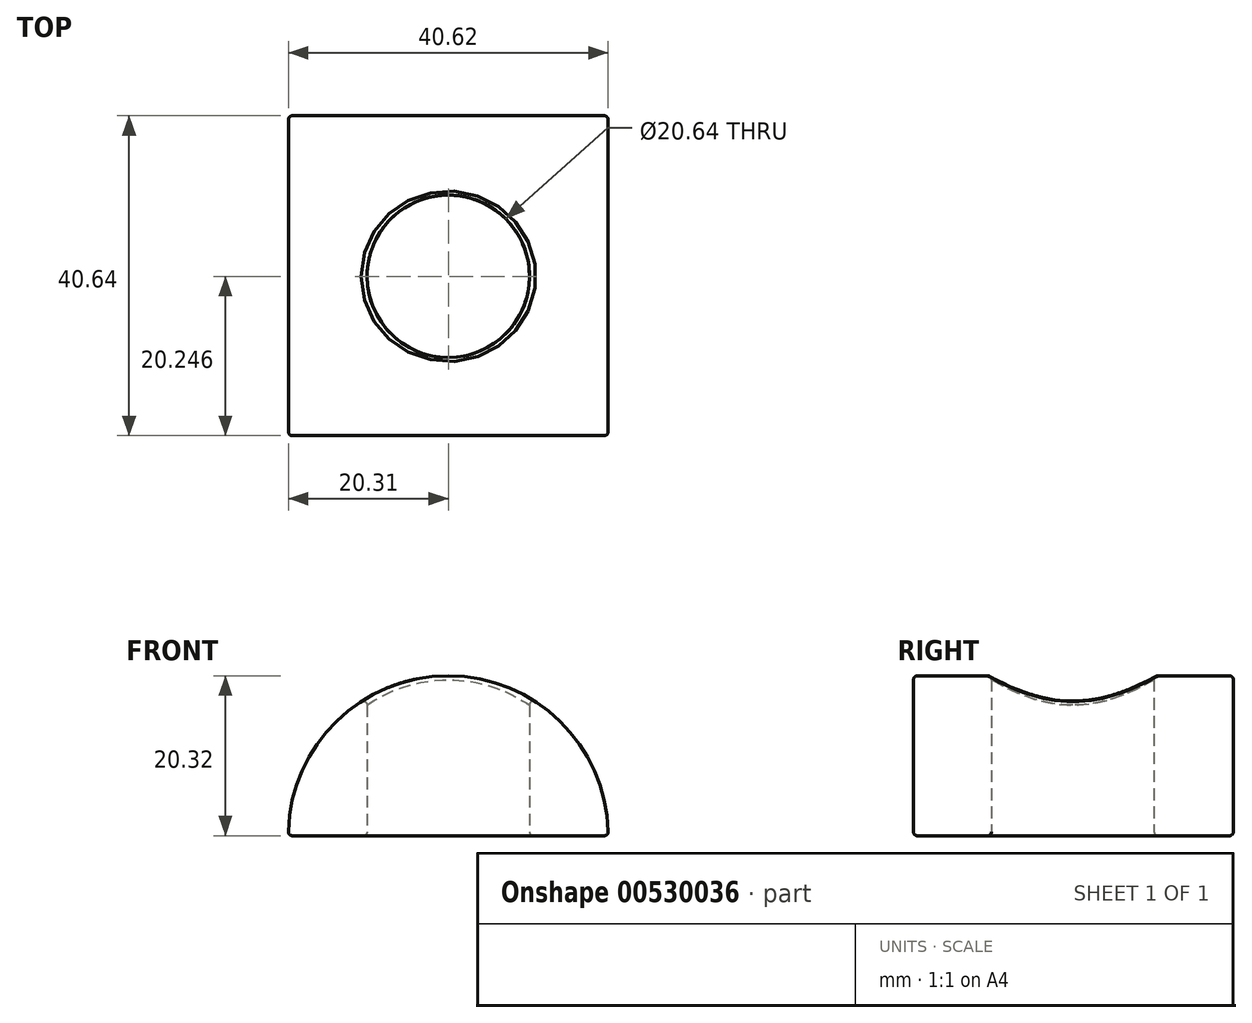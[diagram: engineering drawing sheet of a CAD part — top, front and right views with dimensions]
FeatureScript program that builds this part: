
annotation { "Feature Type Name" : "Feature", "Feature Type Description" : "" }
export const myFeature = defineFeature(function(context is Context, id is Id, definition is map)
    precondition{}
    {
        {
            var Q0;
            Q0=qCreatedBy(makeId("Front.planeOp"),FACE);
            var sketch = newSketch(context, id + "F0", { "sketchPlane" : qUnion([Q0])});
            skLineSegment(sketch, "E0", {"start": v(-20.32, 0) * mm, "end": v(-20.32, 0) * mm});
            skLineSegment(sketch, "E1", {"start": v(20.32, 0) * mm, "end": v(20.32, 0) * mm});
            skLineSegment(sketch, "E2", {"start": v(-20.32, 0) * mm, "end": v(0, 0) * mm, "construction": true});
            skArc(sketch, "E3", {"start": v(20.32, 0) * mm, "mid": v(0, 20.32) * mm, "end": v(-20.32, 0) * mm});
            skLineSegment(sketch, "E4", {"start": v(0, 0) * mm, "end": v(20.32, 0) * mm, "construction": true});
            skLineSegment(sketch, "E5", {"start": v(-20.32, 0) * mm, "end": v(20.32, 0) * mm});
            skSolve(sketch);
        }
        {
            var Q0;
            Q0=qSketchRegion(id+"F0",true);
            extrude(context, id + "F1", {"entities" : qUnion([Q0]), "depth" : 40.64 * mm});
        }
        {
            var Q0;
            Q0=qCreatedBy(makeId("Top.planeOp"),FACE);
            var sketch = newSketch(context, id + "F2", { "sketchPlane" : qUnion([Q0])});
            skLineSegment(sketch, "E6", {"start": v(0, 0) * mm, "end": v(0, -40.79) * mm, "construction": true});
            skCircle(sketch, "E7", {"center": v(0, -20.4) * mm, "radius": 10.32 * mm});
            skSolve(sketch);
        }
        {
            var Q0;
            Q0=qSketchRegion(id+"F2",true);
            extrude(context, id + "F3", {"entities" : qUnion([Q0]), "operationType" : NewBodyOperationType.REMOVE, "endBound" : BoundingType.THROUGH_ALL, "depth" : 25.4 * mm});
        }
        {
            var Q0;
            Q0=makeQuery(id+"F1.opExtrude","CAP_FACE",FACE,{"disambiguationData":[OSD([sQuery(id+"F0.wireOp",EDGE,"E3"),sQuery(id+"F0.wireOp",EDGE,"E5")])],"isStart":true});
            var Q1;
            Q1=makeQuery(id+"F1.opExtrude","SWEPT_FACE",FACE,{"disambiguationData":[OSD([sQuery(id+"F0.wireOp",EDGE,"E5")])]});
            var Q2;
            Q2=makeQuery(id+"F1.opExtrude","SWEPT_FACE",FACE,{"disambiguationData":[OSD([sQuery(id+"F0.wireOp",EDGE,"E3")])]});
            fillet(context, id + "F4", {"entities" : qUnion([Q0, Q1, Q2]), "radius" : 0.5 * mm, "tangentPropagation" : true, "allowEdgeOverflow" : false});
        }
    });
